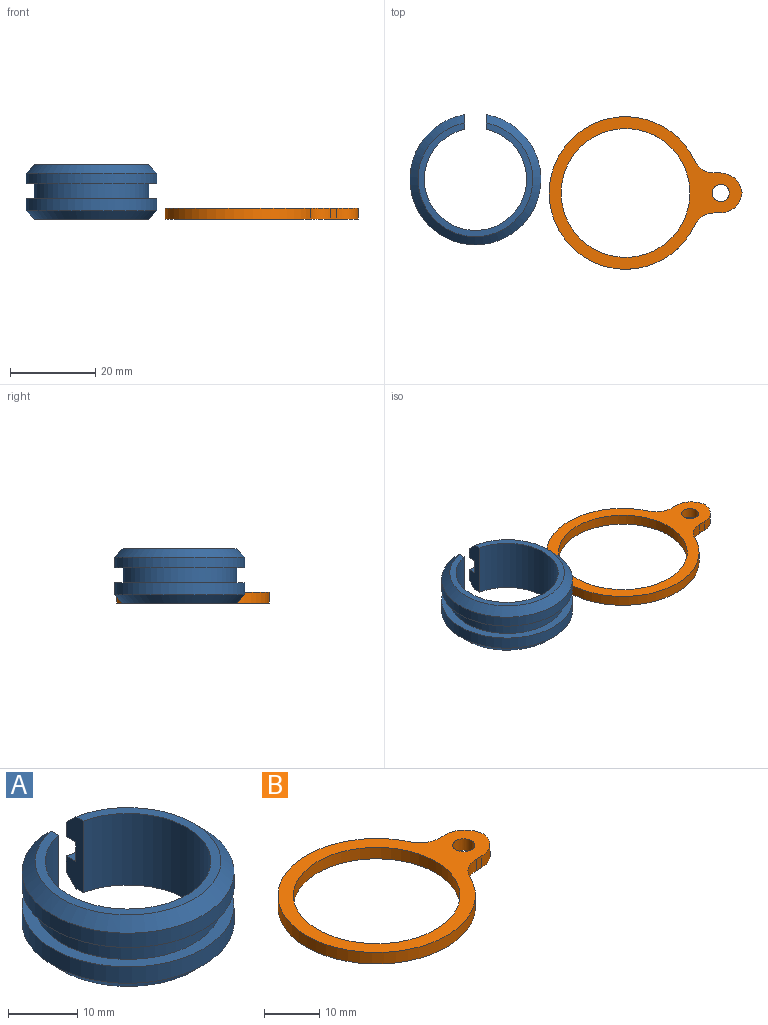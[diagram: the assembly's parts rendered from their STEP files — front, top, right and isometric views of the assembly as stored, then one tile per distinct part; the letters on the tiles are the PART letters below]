
ASSEMBLY  parts=2 mates=1
PART A: 12 faces, bbox 30.7x30.5x12.7 mm
  f0: plane 12.7x3.43mm, normal (1,0,0), area 33.1mm2, adj f1,f3,f4,f5,f6,f7,f8,f9
  f1: cylinder r=15.37mm len=30.73mm, axis (0,0,-1), area 232.3mm2, adj f0,f2,f7,f11
  f2: plane 12.7x3.43mm, normal (-1,0,0), area 33.1mm2, adj f1,f3,f4,f5,f6,f7,f8,f9
  f3: cylinder r=15.37mm len=30.73mm, axis (0,0,-1), area 265.1mm2, adj f0,f2,f9,f10
  f4: cylinder r=12mm len=24mm, axis (0,0,-1), area 892.7mm2, adj f0,f2,f5,f6
  f5: plane 26.92x26.68mm, normal (0,0,1), area 109.4mm2, adj f0,f2,f4,f11
  f6: plane 26.92x26.68mm, normal (0,0,-1), area 109.4mm2, adj f0,f2,f4,f10
  f7: plane 30.73x30.52mm, normal (0,0,-1), area 162.8mm2, adj f0,f1,f2,f8
  f8: cylinder r=13.46mm len=26.92mm, axis (0,0,1), area 274.2mm2, adj f0,f2,f7,f9
  f9: plane 30.73x30.52mm, normal (0,0,1), area 162.8mm2, adj f0,f2,f3,f8
  f10: cone r=15.37mm half-angle=45deg, axis (0,0,1), area 230.2mm2, adj f0,f2,f3,f6
  f11: cone r=13.46mm half-angle=45deg, axis (0,0,-1), area 230.2mm2, adj f0,f1,f2,f5
PART B: 11 faces, bbox 45.2x35.8x2.5 mm
  f0: plane 2.54x1.46mm, normal (0,1,0), area 3.7mm2, adj f5,f6,f7,f9
  f1: cylinder r=17.91mm len=35.81mm, axis (0,0,-1), area 245.8mm2, adj f5,f6,f7,f8
  f2: plane 2.54x1.46mm, normal (0,-1,0), area 3.7mm2, adj f5,f6,f8,f10
  f3: cylinder r=15.11mm len=30.23mm, axis (0,0,-1), area 241.2mm2, adj f5,f6
  f4: cylinder r=2.01mm len=4.02mm, axis (0,0,-1), area 32.1mm2, adj f5,f6
  f5: plane 45.24x35.81mm, normal (0,0,1), area 360.8mm2, adj f0,f1,f2,f3,f4,f7,f8,f9
  f6: plane 45.24x35.81mm, normal (0,0,-1), area 360.8mm2, adj f0,f1,f2,f3,f4,f7,f8,f9
  f7: cylinder r=5.08mm len=4.6mm, axis (0,0,-1), area 14.6mm2, adj f0,f1,f5,f6
  f8: cylinder r=5.08mm len=4.6mm, axis (0,0,-1), area 14.6mm2, adj f1,f2,f5,f6
  f9: cylinder r=5.08mm len=5.07mm, axis (0,0,-1), area 19.3mm2, adj f0,f5,f6,f10
  f10: cylinder r=5.08mm len=5.07mm, axis (0,0,1), area 19.3mm2, adj f2,f5,f6,f9
PLACE A t=(-9.07,-2.04,-0.55)mm
PLACE B t=(26.15,-5.24,-0.55)mm
MATE planar B.f6 <-> A.f6  axis (0,0,-1) through (30.42,-5.24,-0.55)mm
